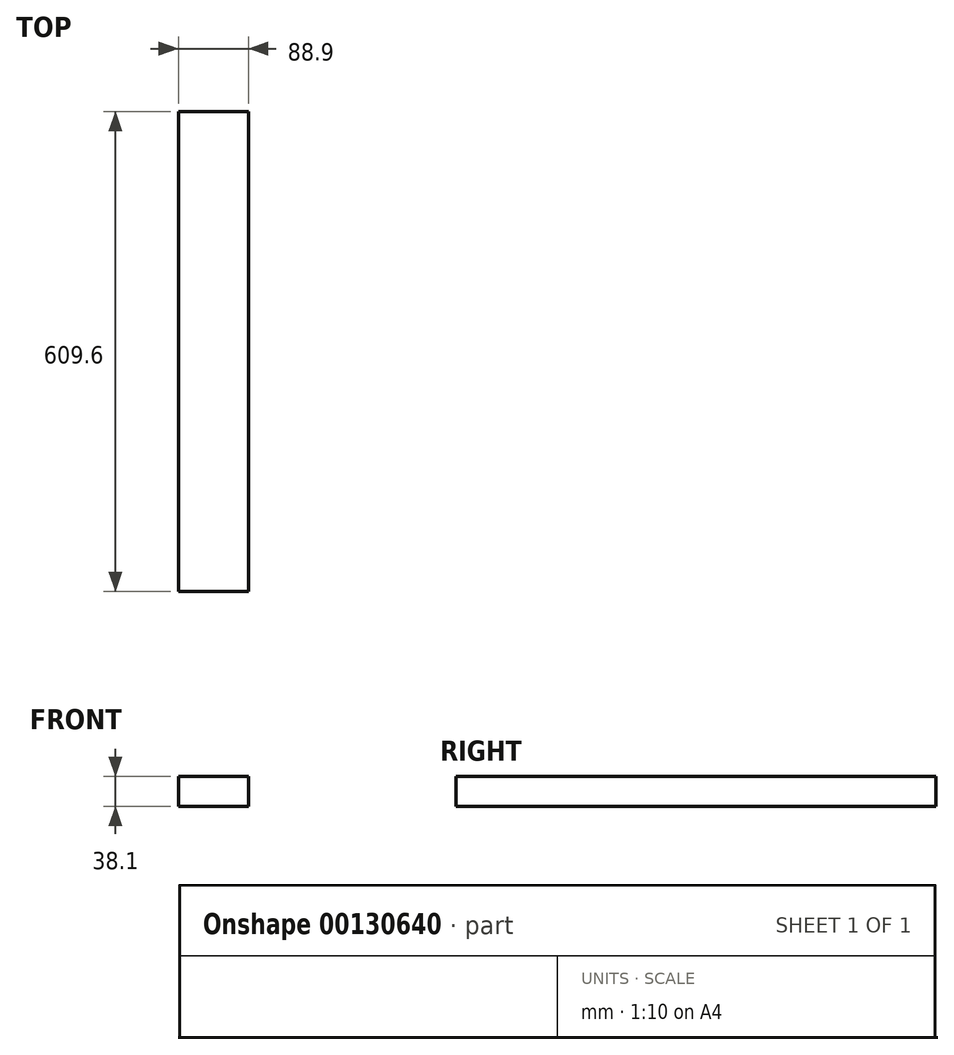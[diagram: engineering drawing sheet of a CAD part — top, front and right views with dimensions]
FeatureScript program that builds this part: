
annotation { "Feature Type Name" : "Feature", "Feature Type Description" : "" }
export const myFeature = defineFeature(function(context is Context, id is Id, definition is map)
    precondition{}
    {
        {
            var Q0;
            Q0=qCreatedBy(makeId("Top.planeOp"),FACE);
            var sketch = newSketch(context, id + "F0", { "sketchPlane" : qUnion([Q0])});
            skLineSegment(sketch, "E0.bottom", {"start": v(0, 0) * mm, "end": v(-88.9, 0) * mm});
            skLineSegment(sketch, "E0.top", {"start": v(0, 609.6) * mm, "end": v(-88.9, 609.6) * mm});
            skLineSegment(sketch, "E0.left", {"start": v(0, 0) * mm, "end": v(0, 609.6) * mm});
            skLineSegment(sketch, "E0.right", {"start": v(-88.9, 0) * mm, "end": v(-88.9, 609.6) * mm});
            skSolve(sketch);
        }
        {
            var Q0;
            Q0=makeQuery(id+"F0.imprint","IMPRINT",FACE,{"disambiguationData":[TD([[makeQuery(id+"F0.imprint","IMPRINT",EDGE,{"derivedFrom":sQuery(id+"F0.wireOp",EDGE,"E0.bottom")}),-1.0]])]});
            extrude(context, id + "F1", {"entities" : qUnion([Q0]), "depth" : 38.1 * mm});
        }
    });
